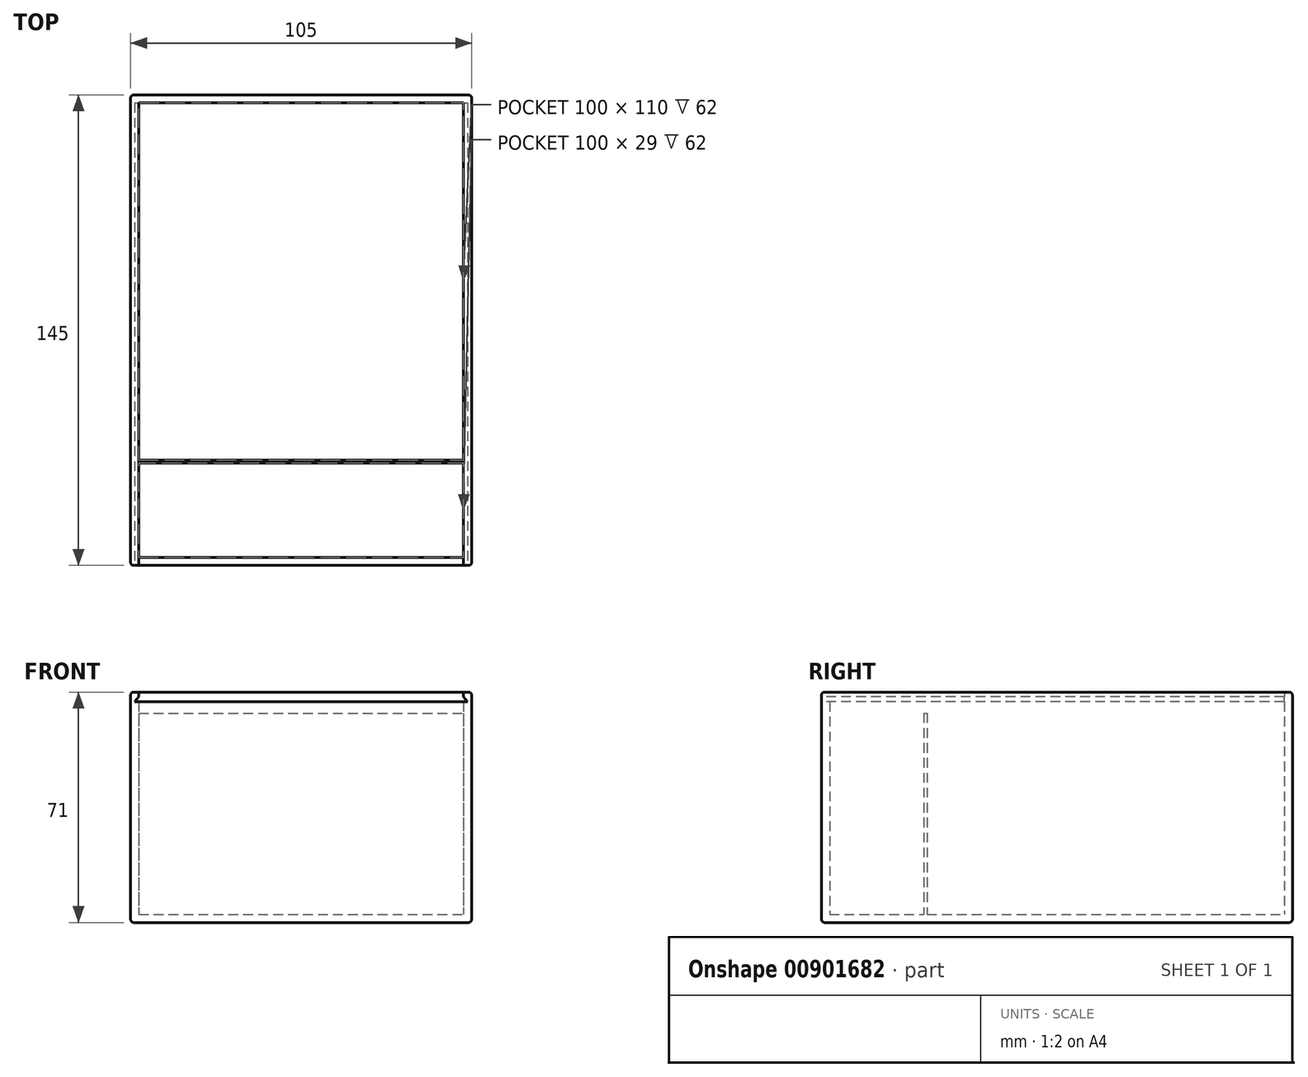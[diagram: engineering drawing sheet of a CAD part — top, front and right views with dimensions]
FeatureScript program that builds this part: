
annotation { "Feature Type Name" : "Feature", "Feature Type Description" : "" }
export const myFeature = defineFeature(function(context is Context, id is Id, definition is map)
    precondition{}
    {
        {
            var Q0;
            Q0=qCreatedBy(makeId("Top.planeOp"),FACE);
            var sketch = newSketch(context, id + "F0", { "sketchPlane" : qUnion([Q0])});
            skLineSegment(sketch, "E0.bottom", {"start": v(-52.5, -72.5) * mm, "end": v(52.5, -72.5) * mm});
            skLineSegment(sketch, "E0.top", {"start": v(-52.5, 72.5) * mm, "end": v(52.5, 72.5) * mm});
            skLineSegment(sketch, "E0.left", {"start": v(-52.5, -72.5) * mm, "end": v(-52.5, 72.5) * mm});
            skLineSegment(sketch, "E0.right", {"start": v(52.5, -72.5) * mm, "end": v(52.5, 72.5) * mm});
            skPoint(sketch, "E0.middle", {"position": v(0, 0) * mm});
            skSolve(sketch);
        }
        {
            var Q0;
            Q0=makeQuery(id+"F0.imprint","IMPRINT",FACE,{"disambiguationData":[TD([[makeQuery(id+"F0.imprint","IMPRINT",EDGE,{"derivedFrom":sQuery(id+"F0.wireOp",EDGE,"E0.bottom")}),1.0]])]});
            extrude(context, id + "F1", {"entities" : qUnion([Q0]), "depth" : 71 * mm, "offsetDistance" : 25 * mm});
        }
        {
            var Q0;
            Q0=makeQuery(id+"F1.opExtrude","CAP_FACE",FACE,{"disambiguationData":[OSD([sQuery(id+"F0.wireOp",EDGE,"E0.bottom"),sQuery(id+"F0.wireOp",EDGE,"E0.top"),sQuery(id+"F0.wireOp",EDGE,"E0.left"),sQuery(id+"F0.wireOp",EDGE,"E0.right")])],"isStart":false});
            shell(context, id + "F2", {"entities" : qUnion([Q0]), "thickness" : 2.5 * mm});
        }
        {
            var Q0;
            Q0=makeQuery(id+"F2.opShell","OFFSET_FACE",FACE,{"disambiguationData":[OSD([sQuery(id+"F0.wireOp",EDGE,"E0.bottom"),sQuery(id+"F0.wireOp",EDGE,"E0.top"),sQuery(id+"F0.wireOp",EDGE,"E0.left"),sQuery(id+"F0.wireOp",EDGE,"E0.right")])]});
            var sketch = newSketch(context, id + "F3", { "sketchPlane" : qUnion([Q0])});
            skLineSegment(sketch, "E1.bottom", {"start": v(-50, -41) * mm, "end": v(50, -41) * mm});
            skLineSegment(sketch, "E1.top", {"start": v(-50, -40) * mm, "end": v(50, -40) * mm});
            skLineSegment(sketch, "E1.left", {"start": v(-50, -40) * mm, "end": v(-50, -41) * mm});
            skLineSegment(sketch, "E1.right", {"start": v(50, -40) * mm, "end": v(50, -41) * mm});
            skLineSegment(sketch, "E2.bottom", {"start": v(-0.5, -41) * mm, "end": v(0.5, -41) * mm});
            skLineSegment(sketch, "E2.top", {"start": v(-0.5, -70) * mm, "end": v(0.5, -70) * mm});
            skLineSegment(sketch, "E2.left", {"start": v(-0.5, -41) * mm, "end": v(-0.5, -70) * mm});
            skLineSegment(sketch, "E2.right", {"start": v(0.5, -41) * mm, "end": v(0.5, -70) * mm});
            skSolve(sketch);
        }
        {
            var Q0;
            Q0=makeQuery(id+"F3.imprint","IMPRINT",FACE,{"disambiguationData":[TD([[makeQuery(id+"F3.imprint","IMPRINT",EDGE,{"derivedFrom":sQuery(id+"F3.wireOp",EDGE,"E1.top")}),-1.0]])]});
            var Q1;
            Q1=makeQuery(id+"F3.imprint","IMPRINT",FACE,{"disambiguationData":[TD([[makeQuery(id+"F3.imprint","IMPRINT",EDGE,{"derivedFrom":sQuery(id+"F3.wireOp",EDGE,"E2.bottom")}),-1.0]])]});
            extrude(context, id + "F4", {"entities" : qUnion([Q0, Q1]), "operationType" : NewBodyOperationType.ADD, "depth" : 62 * mm, "offsetDistance" : 25 * mm});
        }
        {
            var Q0;
            Q0=makeQuery(id+"F1.opExtrude","SWEPT_FACE",FACE,{"disambiguationData":[OSD([sQuery(id+"F0.wireOp",EDGE,"E0.bottom")])]});
            var sketch = newSketch(context, id + "F5", { "sketchPlane" : qUnion([Q0])});
            skLineSegment(sketch, "E3.bottom", {"start": v(0, 71) * mm, "end": v(50, 71) * mm});
            skLineSegment(sketch, "E3.top", {"start": v(0, 69.5) * mm, "end": v(50, 69.5) * mm});
            skLineSegment(sketch, "E3.left", {"start": v(0, 71) * mm, "end": v(0, 69.5) * mm});
            skLineSegment(sketch, "E3.right", {"start": v(50, 71) * mm, "end": v(50, 69.5) * mm});
            skLineSegment(sketch, "E4", {"start": v(0, 69.5) * mm, "end": v(0, 68) * mm});
            skLineSegment(sketch, "E5", {"start": v(0, 68) * mm, "end": v(51.2, 68) * mm});
            skLineSegment(sketch, "E6", {"start": v(51.2, 68) * mm, "end": v(50, 69.5) * mm});
            skLineSegment(sketch, "E7.MirrorCS", {"start": v(-51.2, 68) * mm, "end": v(-50, 69.5) * mm});
            skLineSegment(sketch, "E8.MirrorCS", {"start": v(-50, 71) * mm, "end": v(-50, 69.5) * mm});
            skLineSegment(sketch, "E9.MirrorCS", {"start": v(0, 69.5) * mm, "end": v(-50, 69.5) * mm});
            skLineSegment(sketch, "E10.MirrorCS", {"start": v(0, 68) * mm, "end": v(-51.2, 68) * mm});
            skLineSegment(sketch, "E11.MirrorCS", {"start": v(0, 71) * mm, "end": v(-50, 71) * mm});
            skSolve(sketch);
        }
        {
            var Q0;
            Q0 = qSketchRegion(id + "F5", true);
            var Q1;
            Q1=makeQuery(id+"F2.opShell","OFFSET_FACE",FACE,{"disambiguationData":[OSD([sQuery(id+"F0.wireOp",EDGE,"E0.top")])]});
            extrude(context, id + "F6", {"entities" : qUnion([Q0]), "operationType" : NewBodyOperationType.REMOVE, "endBound" : BoundingType.UP_TO_SURFACE, "oppositeDirection" : true, "depth" : 25 * mm, "endBoundEntityFace" : qUnion([Q1]), "offsetDistance" : 25 * mm, "hasSecondDirection" : true, "secondDirectionBound" : SecondDirectionBoundingType.THROUGH_ALL, "secondDirectionOppositeDirection" : false, "secondDirectionDepth" : 25 * mm});
        }
        {
            var Q0;
            Q0=makeQuery(id+"F1.opExtrude","SWEPT_FACE",FACE,{"disambiguationData":[OSD([sQuery(id+"F0.wireOp",EDGE,"E0.right")])]});
            var Q1;
            Q1=makeQuery(id+"F1.opExtrude","SWEPT_FACE",FACE,{"disambiguationData":[OSD([sQuery(id+"F0.wireOp",EDGE,"E0.left")])]});
            var Q2;
            Q2=makeQuery(id+"F1.opExtrude","SWEPT_FACE",FACE,{"disambiguationData":[OSD([sQuery(id+"F0.wireOp",EDGE,"E0.top")])]});
            var Q3;
            Q3=makeQuery(id+"F1.opExtrude","CAP_EDGE",EDGE,{"disambiguationData":[OSD([sQuery(id+"F0.wireOp",EDGE,"E0.bottom")])],"isStart":true});
            var Q4;
            {var subQ0=sQuery(id+"F0.wireOp",EDGE,"E0.left");var subQ1=sQuery(id+"F0.wireOp",EDGE,"E0.bottom");Q4=makeQuery(id+"F6.boolean.opBoolean","SPLIT",EDGE,{"disambiguationData":[TD([makeQuery(id+"F1.opExtrude","SWEPT_FACE",FACE,{"disambiguationData":[OSD([subQ0])]})])],"derivedFrom":makeQuery(id+"F1.opExtrude","CAP_EDGE",EDGE,{"disambiguationData":[OSD([subQ1])],"isStart":false})});}
            var Q5;
            {var subQ0=sQuery(id+"F0.wireOp",EDGE,"E0.right");var subQ1=sQuery(id+"F0.wireOp",EDGE,"E0.bottom");Q5=makeQuery(id+"F6.boolean.opBoolean","SPLIT",EDGE,{"disambiguationData":[TD([makeQuery(id+"F1.opExtrude","SWEPT_FACE",FACE,{"disambiguationData":[OSD([subQ0])]})])],"derivedFrom":makeQuery(id+"F1.opExtrude","CAP_EDGE",EDGE,{"disambiguationData":[OSD([subQ1])],"isStart":false})});}
            fillet(context, id + "F7", {"entities" : qUnion([Q0, Q1, Q2, Q3, Q4, Q5]), "radius" : 1 * mm, "tangentPropagation" : true, "allowEdgeOverflow" : false});
        }
    });
